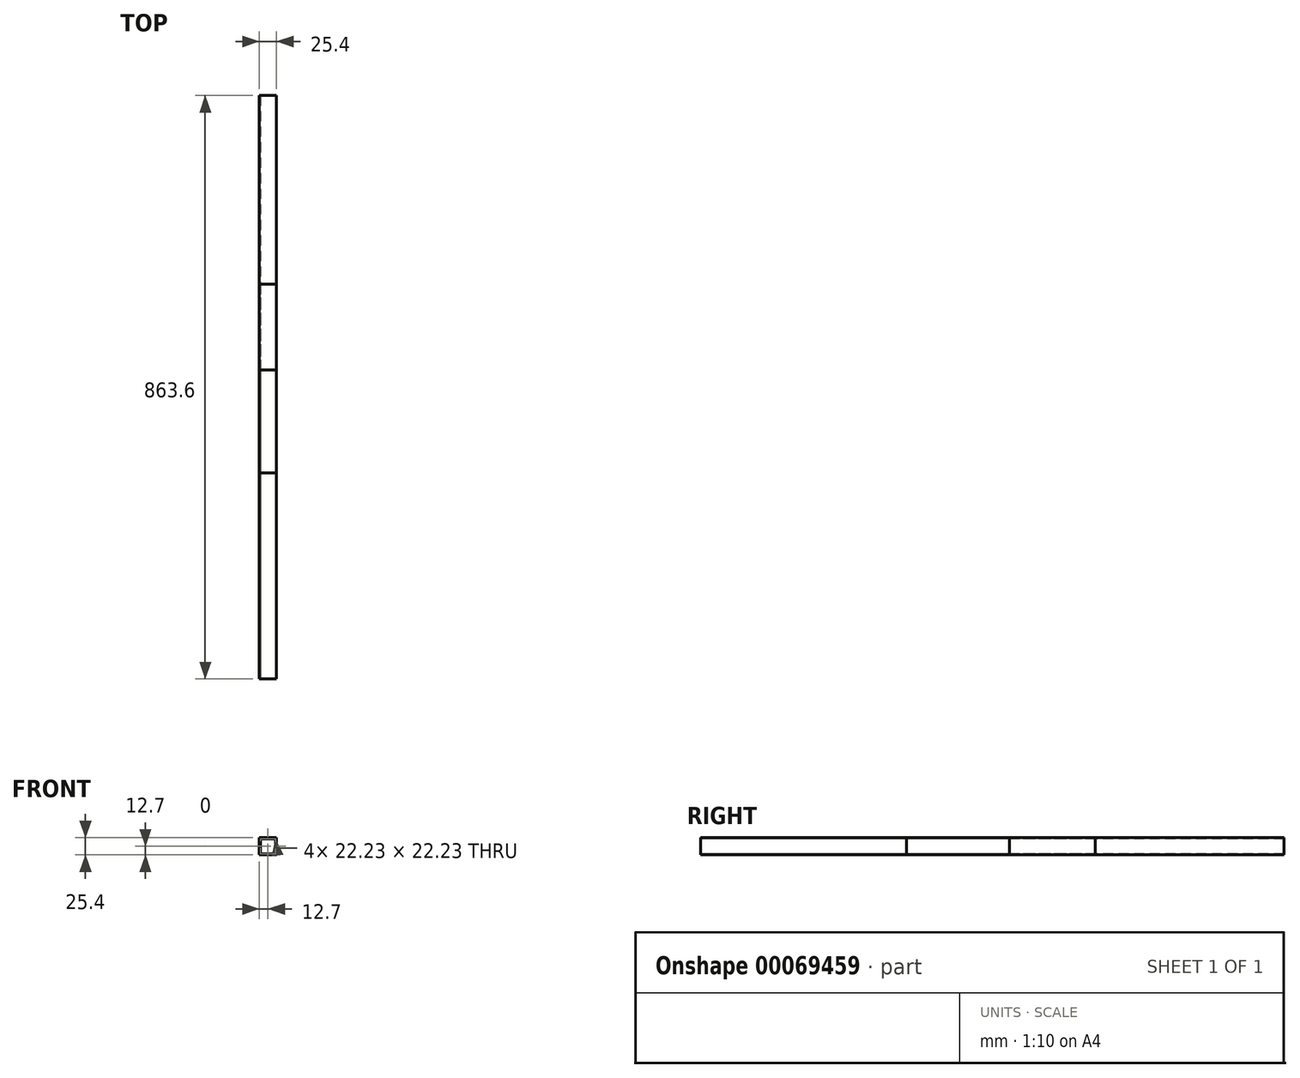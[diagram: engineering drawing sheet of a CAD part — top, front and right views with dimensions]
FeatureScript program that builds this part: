
annotation { "Feature Type Name" : "Feature", "Feature Type Description" : "" }
export const myFeature = defineFeature(function(context is Context, id is Id, definition is map)
    precondition{}
    {
        {
            var Q0;
            Q0=qCreatedBy(makeId("Front.planeOp"),FACE);
            var sketch = newSketch(context, id + "F0", { "sketchPlane" : qUnion([Q0])});
            skLineSegment(sketch, "E0.rect.bottom", {"start": v(12.7, -12.7) * mm, "end": v(-12.7, -12.7) * mm});
            skLineSegment(sketch, "E0.rect.top", {"start": v(12.7, 12.7) * mm, "end": v(-12.7, 12.7) * mm});
            skLineSegment(sketch, "E0.rect.left", {"start": v(12.7, -12.7) * mm, "end": v(12.7, 12.7) * mm});
            skLineSegment(sketch, "E0.rect.right", {"start": v(-12.7, -12.7) * mm, "end": v(-12.7, 12.7) * mm});
            skPoint(sketch, "E0.rect.middle", {"position": v(0, 0) * mm});
            skLineSegment(sketch, "E1.0", {"start": v(-11.11, -11.11) * mm, "end": v(-11.11, 11.11) * mm});
            skLineSegment(sketch, "E1.1", {"start": v(11.11, -11.11) * mm, "end": v(-11.11, -11.11) * mm});
            skLineSegment(sketch, "E1.2", {"start": v(11.11, -11.11) * mm, "end": v(11.11, 11.11) * mm});
            skLineSegment(sketch, "E1.3", {"start": v(11.11, 11.11) * mm, "end": v(-11.11, 11.11) * mm});
            skSolve(sketch);
        }
        {
            var Q0;
            Q0=makeQuery(id+"F0.imprint","IMPRINT",FACE,{"disambiguationData":[TD([[makeQuery(id+"F0.imprint","IMPRINT",EDGE,{"derivedFrom":sQuery(id+"F0.wireOp",EDGE,"E0.rect.bottom")}),-1.0]])]});
            extrude(context, id + "F1", {"entities" : qUnion([Q0]), "oppositeDirection" : true, "depth" : 584.2 * mm});
        }
        {
            var Q0;
            Q0 = qSketchRegion(id + "F0", true);
            extrude(context, id + "F2", {"entities" : qUnion([Q0]), "oppositeDirection" : true, "depth" : 863.6 * mm});
        }
        {
            var Q0;
            Q0 = qSketchRegion(id + "F0", true);
            extrude(context, id + "F3", {"entities" : qUnion([Q0]), "oppositeDirection" : true, "depth" : 304.8 * mm});
        }
        {
            var Q0;
            Q0 = qSketchRegion(id + "F0", true);
            extrude(context, id + "F4", {"entities" : qUnion([Q0]), "oppositeDirection" : true, "depth" : 457.2 * mm});
        }
    });
